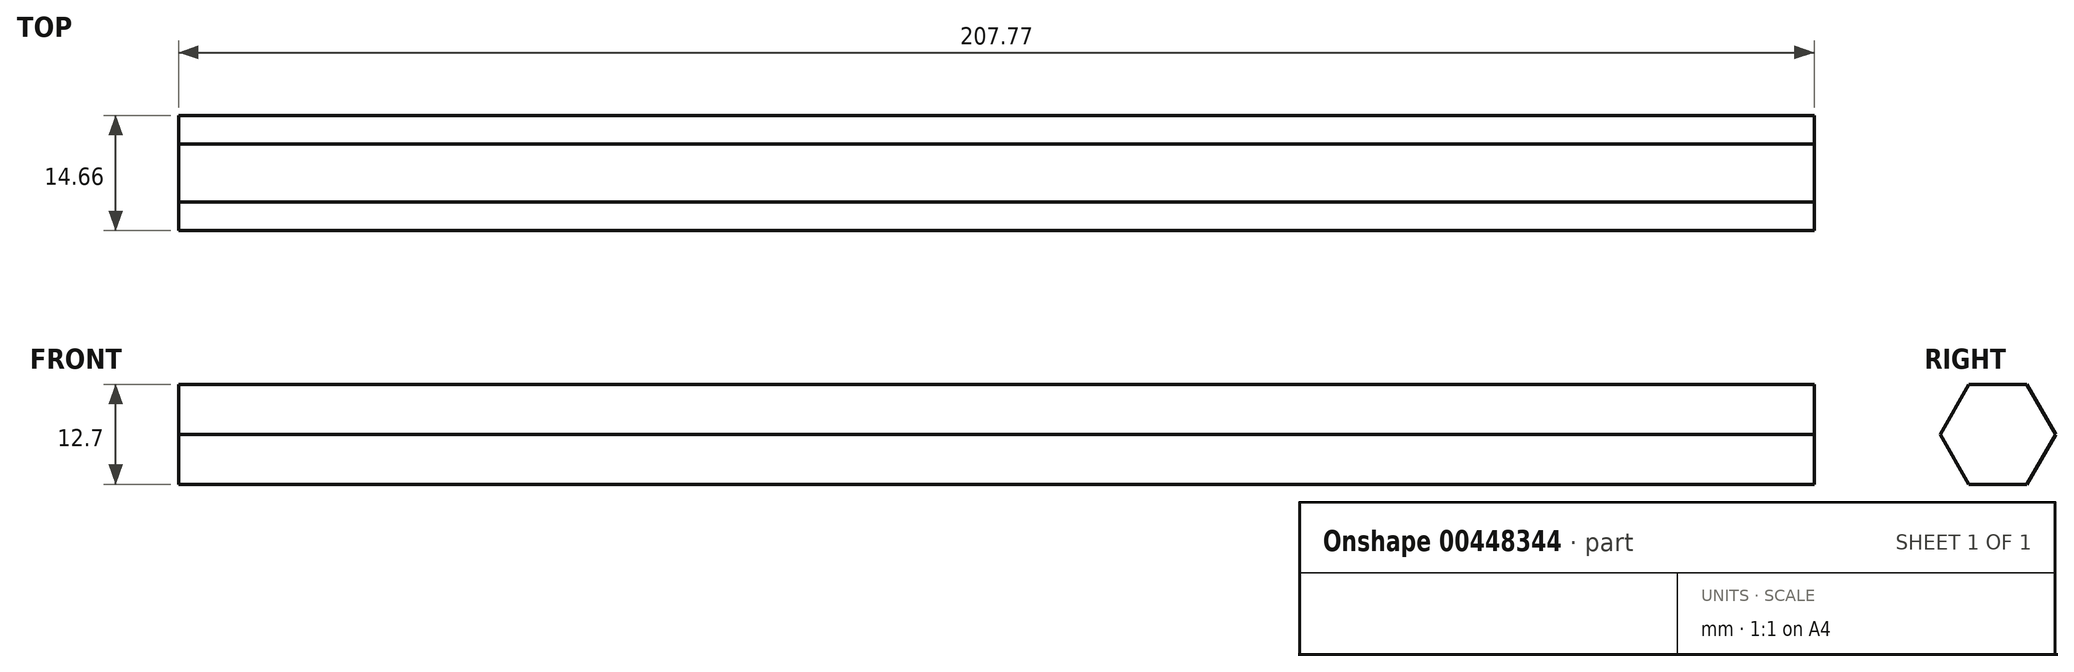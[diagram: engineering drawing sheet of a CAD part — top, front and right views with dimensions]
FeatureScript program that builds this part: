
annotation { "Feature Type Name" : "Feature", "Feature Type Description" : "" }
export const myFeature = defineFeature(function(context is Context, id is Id, definition is map)
    precondition{}
    {
        {
            var Q0;
            Q0=qCreatedBy(makeId("Right.planeOp"),FACE);
            var sketch = newSketch(context, id + "F0", { "sketchPlane" : qUnion([Q0])});
            skCircle(sketch, "E0.cCircle", {"center": v(0, 0) * mm, "radius": 6.35 * mm, "construction": true});
            skLineSegment(sketch, "E0.0", {"start": v(-3.67, 6.35) * mm, "end": v(3.67, 6.35) * mm});
            skLineSegment(sketch, "E0.1", {"start": v(3.67, 6.35) * mm, "end": v(7.33, 0) * mm});
            skLineSegment(sketch, "E0.2", {"start": v(7.33, 0) * mm, "end": v(3.67, -6.35) * mm});
            skLineSegment(sketch, "E0.3", {"start": v(3.67, -6.35) * mm, "end": v(-3.67, -6.35) * mm});
            skLineSegment(sketch, "E0.4", {"start": v(-3.67, -6.35) * mm, "end": v(-7.33, 0) * mm});
            skLineSegment(sketch, "E0.5", {"start": v(-7.33, 0) * mm, "end": v(-3.67, 6.35) * mm});
            skPoint(sketch, "E0.0.midPoint", {"position": v(0, 6.35) * mm});
            skSolve(sketch);
        }
        {
            var Q0;
            Q0=makeQuery(id+"F0.imprint","IMPRINT",FACE,{"disambiguationData":[TD([[makeQuery(id+"F0.imprint","IMPRINT",EDGE,{"derivedFrom":sQuery(id+"F0.wireOp",EDGE,"E0.0")}),-1.0]])]});
            extrude(context, id + "F1", {"entities" : qUnion([Q0]), "depth" : 207.77 * mm, "offsetDistance" : 25.4 * mm});
        }
    });
